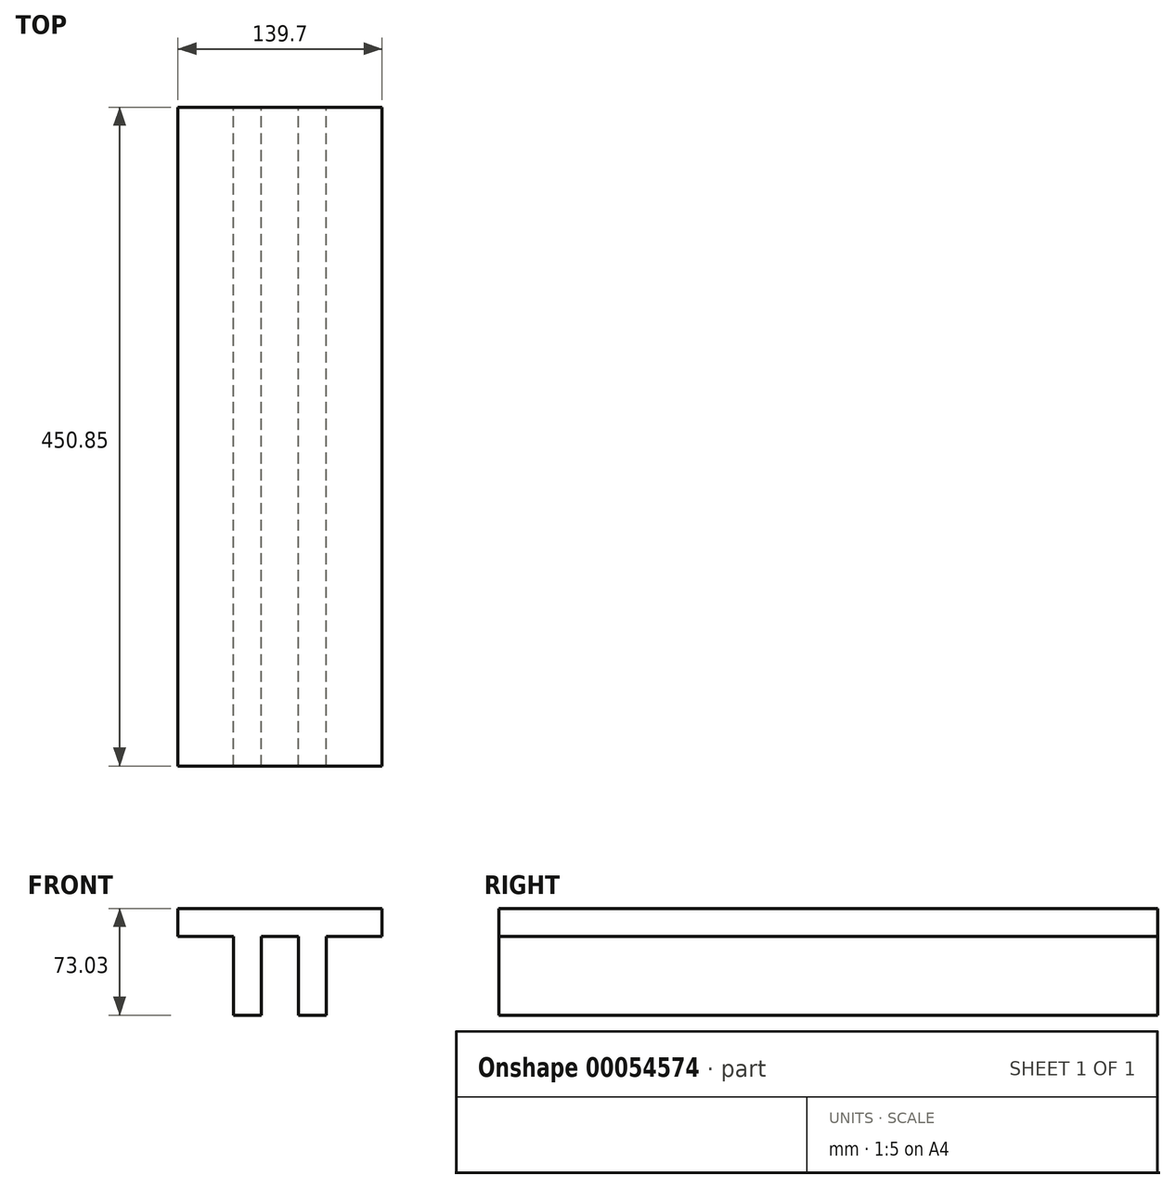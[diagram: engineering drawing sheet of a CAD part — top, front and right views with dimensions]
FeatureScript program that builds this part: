
annotation { "Feature Type Name" : "Feature", "Feature Type Description" : "" }
export const myFeature = defineFeature(function(context is Context, id is Id, definition is map)
    precondition{}
    {
        {
            var Q0;
            Q0=qCreatedBy(makeId("Front.planeOp"),FACE);
            var sketch = newSketch(context, id + "F0", { "sketchPlane" : qUnion([Q0])});
            skLineSegment(sketch, "E0.bottom", {"start": v(0, 0) * mm, "end": v(139.7, 0) * mm});
            skLineSegment(sketch, "E0.top", {"start": v(0, 19.05) * mm, "end": v(139.7, 19.05) * mm});
            skLineSegment(sketch, "E0.left", {"start": v(0, 0) * mm, "end": v(0, 19.05) * mm});
            skLineSegment(sketch, "E0.right", {"start": v(139.7, 0) * mm, "end": v(139.7, 19.05) * mm});
            skSolve(sketch);
        }
        {
            var Q0;
            Q0=makeQuery(id+"F0.imprint","IMPRINT",FACE,{"disambiguationData":[TD([[makeQuery(id+"F0.imprint","IMPRINT",EDGE,{"derivedFrom":sQuery(id+"F0.wireOp",EDGE,"E0.bottom")}),1.0]])]});
            extrude(context, id + "F1", {"entities" : qUnion([Q0]), "depth" : 450.85 * mm});
        }
        {
            var Q0;
            Q0=makeQuery(id+"F1.opExtrude","SWEPT_FACE",FACE,{"disambiguationData":[OSD([sQuery(id+"F0.wireOp",EDGE,"E0.bottom")])]});
            var sketch = newSketch(context, id + "F2", { "sketchPlane" : qUnion([Q0])});
            skLineSegment(sketch, "E1.bottom", {"start": v(101.6, 450.85) * mm, "end": v(82.55, 450.85) * mm});
            skLineSegment(sketch, "E1.top", {"start": v(101.6, 0) * mm, "end": v(82.55, 0) * mm});
            skLineSegment(sketch, "E1.left", {"start": v(101.6, 450.85) * mm, "end": v(101.6, 0) * mm});
            skLineSegment(sketch, "E1.right", {"start": v(82.55, 450.85) * mm, "end": v(82.55, 0) * mm});
            skSolve(sketch);
        }
        {
            var Q0;
            Q0=makeQuery(id+"F2.imprint","IMPRINT",FACE,{"disambiguationData":[TD([[makeQuery(id+"F2.imprint","IMPRINT",EDGE,{"derivedFrom":sQuery(id+"F2.wireOp",EDGE,"E1.bottom")}),-1.0]])]});
            extrude(context, id + "F3", {"entities" : qUnion([Q0]), "operationType" : NewBodyOperationType.ADD, "depth" : 57.15 * mm - 3.17 * mm});
        }
        {
            var Q0;
            {var subQ0=sQuery(id+"F0.wireOp",EDGE,"E0.left");var subQ3=sQuery(id+"F0.wireOp",EDGE,"E0.bottom");Q0=makeQuery(id+"F3.boolean.opBoolean","SPLIT",FACE,{"disambiguationData":[TD([makeQuery(id+"F1.opExtrude","SWEPT_FACE",FACE,{"disambiguationData":[OSD([subQ0])]})])],"derivedFrom":makeQuery(id+"F1.opExtrude","SWEPT_FACE",FACE,{"disambiguationData":[OSD([subQ3])]})});}
            var sketch = newSketch(context, id + "F4", { "sketchPlane" : qUnion([Q0])});
            skLineSegment(sketch, "E2.bottom", {"start": v(38.1, 450.85) * mm, "end": v(57.15, 450.85) * mm});
            skLineSegment(sketch, "E2.top", {"start": v(38.1, 0) * mm, "end": v(57.15, 0) * mm});
            skLineSegment(sketch, "E2.left", {"start": v(38.1, 450.85) * mm, "end": v(38.1, 0) * mm});
            skLineSegment(sketch, "E2.right", {"start": v(57.15, 450.85) * mm, "end": v(57.15, 0) * mm});
            skSolve(sketch);
        }
        {
            var Q0;
            Q0=makeQuery(id+"F4.imprint","IMPRINT",FACE,{"disambiguationData":[TD([[makeQuery(id+"F4.imprint","IMPRINT",EDGE,{"derivedFrom":sQuery(id+"F4.wireOp",EDGE,"E2.bottom")}),-1.0]])]});
            extrude(context, id + "F5", {"entities" : qUnion([Q0]), "operationType" : NewBodyOperationType.ADD, "depth" : 53.97 * mm});
        }
    });
